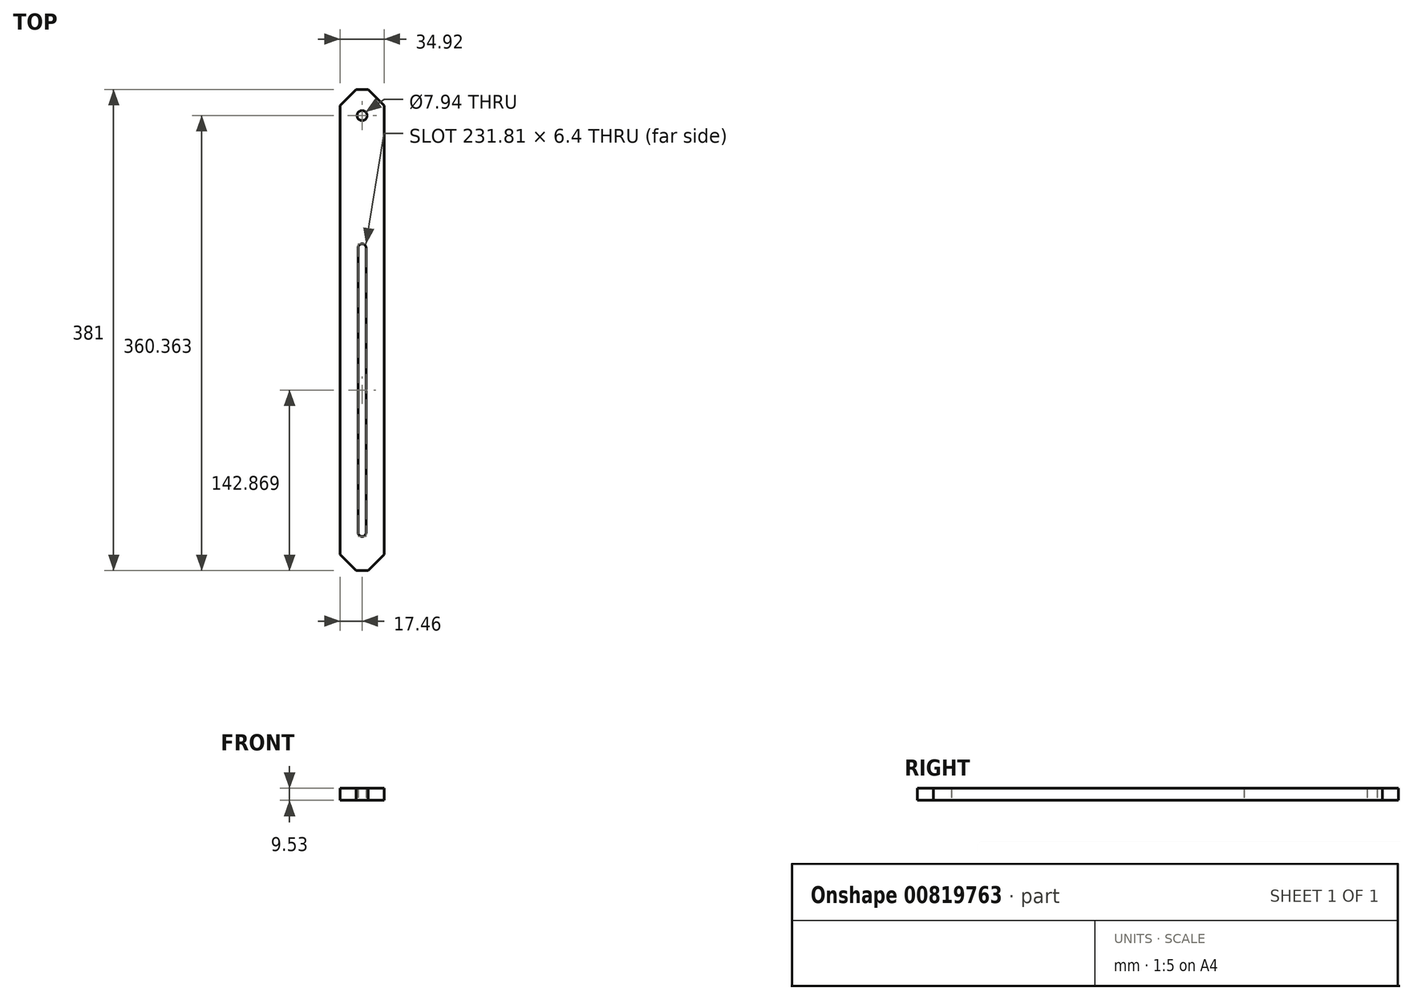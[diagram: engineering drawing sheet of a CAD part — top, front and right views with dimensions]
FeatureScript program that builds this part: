
annotation { "Feature Type Name" : "Feature", "Feature Type Description" : "" }
export const myFeature = defineFeature(function(context is Context, id is Id, definition is map)
    precondition{}
    {
        {
            var Q0;
            Q0=qCreatedBy(makeId("Top.planeOp"),FACE);
            var sketch = newSketch(context, id + "F0", { "sketchPlane" : qUnion([Q0])});
            skLineSegment(sketch, "E0.bottom", {"start": v(-4.76, 190.5) * mm, "end": v(4.76, 190.5) * mm});
            skLineSegment(sketch, "E0.top", {"start": v(-4.76, -190.5) * mm, "end": v(4.76, -190.5) * mm});
            skLineSegment(sketch, "E0.left", {"start": v(-17.46, 177.8) * mm, "end": v(-17.46, -177.8) * mm});
            skLineSegment(sketch, "E0.right", {"start": v(17.46, 177.8) * mm, "end": v(17.46, -177.8) * mm});
            skPoint(sketch, "E0.middle", {"position": v(0, 0) * mm});
            skLineSegment(sketch, "E1", {"start": v(-17.46, 169.86) * mm, "end": v(17.46, 169.86) * mm, "construction": true});
            skLineSegment(sketch, "E2", {"start": v(0, 190.5) * mm, "end": v(0, -190.5) * mm, "construction": true});
            skCircle(sketch, "E3", {"center": v(0, 169.86) * mm, "radius": 3.97 * mm});
            skLineSegment(sketch, "E4", {"start": v(-17.46, -160.34) * mm, "end": v(17.46, -160.34) * mm, "construction": true});
            skLineSegment(sketch, "E5", {"start": v(-17.46, 65.07) * mm, "end": v(17.46, 65.07) * mm, "construction": true});
            skLineSegment(sketch, "E6", {"start": v(-17.46, -177.8) * mm, "end": v(-4.76, -190.5) * mm});
            skLineSegment(sketch, "E7.MirrorCS", {"start": v(17.46, -177.8) * mm, "end": v(4.76, -190.5) * mm});
            skLineSegment(sketch, "E8.MirrorCS", {"start": v(17.46, 177.8) * mm, "end": v(4.76, 190.5) * mm});
            skLineSegment(sketch, "E9.MirrorCS", {"start": v(-17.46, 177.8) * mm, "end": v(-4.76, 190.5) * mm});
            skPoint(sketch, "E10.orphan", {"position": v(-17.46, -190.5) * mm});
            skPoint(sketch, "E11.orphan", {"position": v(17.46, -190.5) * mm});
            skPoint(sketch, "E12.orphan", {"position": v(-17.46, 190.5) * mm});
            skPoint(sketch, "E13.orphan", {"position": v(17.46, 190.5) * mm});
            skPoint(sketch, "E14.center.orphan", {"position": v(0, 65.07) * mm});
            skPoint(sketch, "E15.center.orphan", {"position": v(0, -160.34) * mm});
            skArc(sketch, "E16", {"start": v(-3.2, -160.34) * mm, "mid": v(0, -163.54) * mm, "end": v(3.2, -160.34) * mm});
            skArc(sketch, "E17", {"start": v(3.2, 65.07) * mm, "mid": v(0, 68.28) * mm, "end": v(-3.2, 65.07) * mm});
            skLineSegment(sketch, "E18", {"start": v(-3.2, 65.07) * mm, "end": v(-3.2, -160.34) * mm});
            skLineSegment(sketch, "E19", {"start": v(3.2, -160.34) * mm, "end": v(3.2, 65.07) * mm});
            skSolve(sketch);
        }
        {
            var Q0;
            Q0=makeQuery(id+"F0.imprint","IMPRINT",FACE,{"disambiguationData":[TD([[makeQuery(id+"F0.imprint","IMPRINT",EDGE,{"derivedFrom":sQuery(id+"F0.wireOp",EDGE,"E0.bottom")}),-1.0]])]});
            extrude(context, id + "F1", {"entities" : qUnion([Q0]), "depth" : 9.52 * mm, "offsetDistance" : 25.4 * mm});
        }
    });
